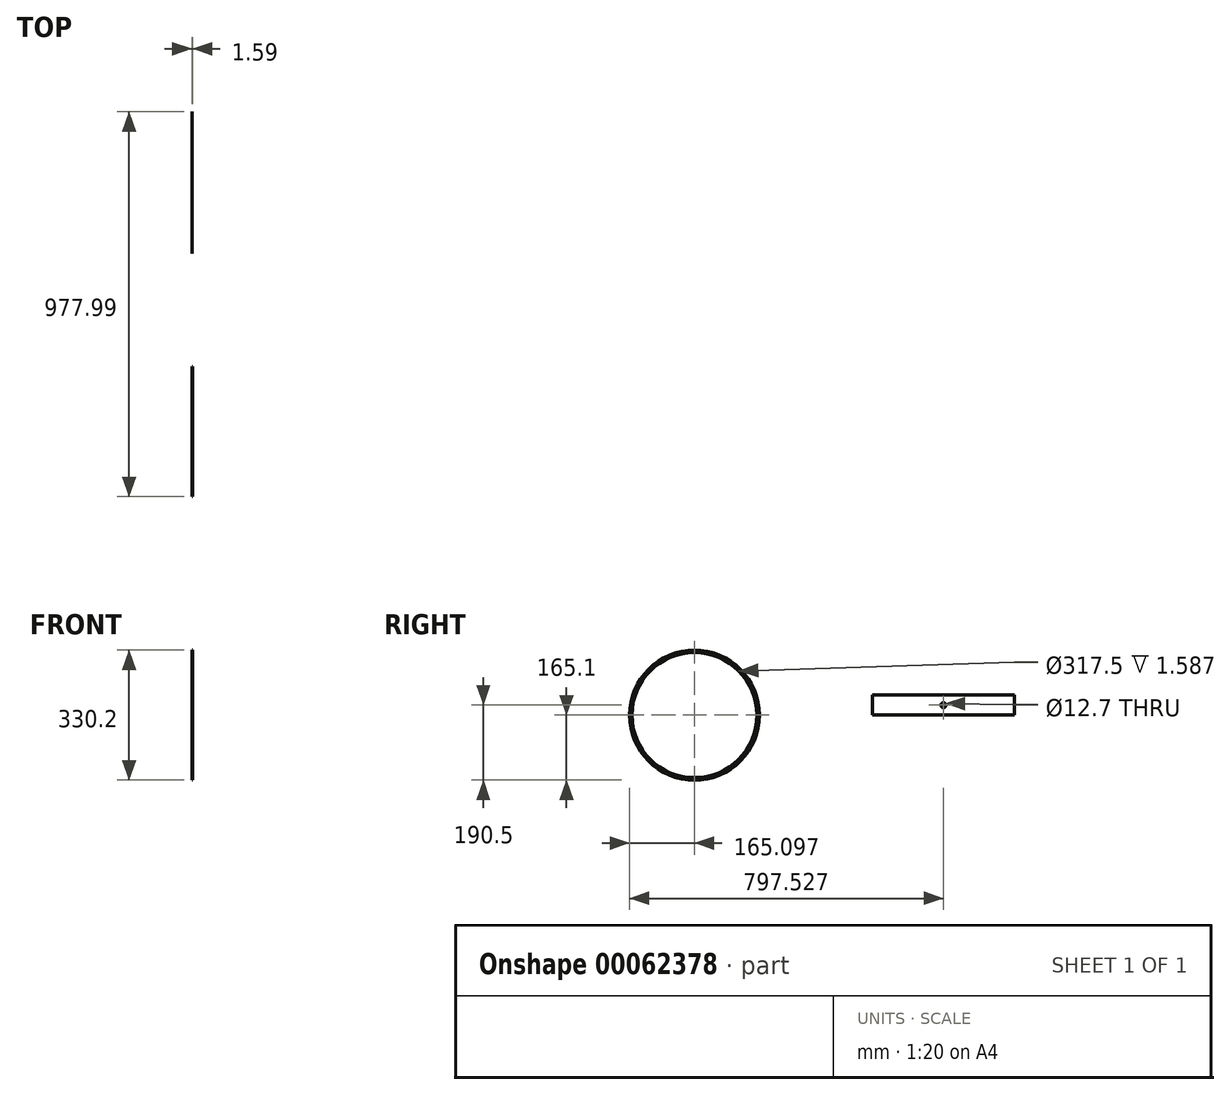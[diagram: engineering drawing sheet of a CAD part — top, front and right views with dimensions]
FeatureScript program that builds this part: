
annotation { "Feature Type Name" : "Feature", "Feature Type Description" : "" }
export const myFeature = defineFeature(function(context is Context, id is Id, definition is map)
    precondition{}
    {
        {
            var Q0;
            Q0=qCreatedBy(makeId("Right.planeOp"),FACE);
            var sketch = newSketch(context, id + "F0", { "sketchPlane" : qUnion([Q0])});
            skLineSegment(sketch, "E0.bottom", {"start": v(0, 0) * mm, "end": v(360.93, 0) * mm});
            skLineSegment(sketch, "E0.top", {"start": v(0, 50.8) * mm, "end": v(360.93, 50.8) * mm});
            skLineSegment(sketch, "E0.left", {"start": v(0, 0) * mm, "end": v(0, 50.8) * mm});
            skLineSegment(sketch, "E0.right", {"start": v(360.93, 0) * mm, "end": v(360.93, 50.8) * mm});
            skCircle(sketch, "E1", {"center": v(180.47, 25.4) * mm, "radius": 6.35 * mm});
            skPoint(sketch, "E1.centerSnap0", {"position": v(0, 25.4) * mm});
            skPoint(sketch, "E1.centerSnap1", {"position": v(180.47, 50.8) * mm});
            skSolve(sketch);
        }
        {
            var Q0;
            Q0=makeQuery(id+"F0.imprint","IMPRINT",FACE,{"disambiguationData":[TD([[makeQuery(id+"F0.imprint","IMPRINT",EDGE,{"derivedFrom":sQuery(id+"F0.wireOp",EDGE,"E0.bottom")}),1.0]])]});
            extrude(context, id + "F1", {"entities" : qUnion([Q0]), "depth" : 0.25 * mm});
        }
        {
            var Q0;
            Q0=qCreatedBy(makeId("Right.planeOp"),FACE);
            var sketch = newSketch(context, id + "F2", { "sketchPlane" : qUnion([Q0])});
            skCircle(sketch, "E2", {"center": v(-451.96, 0) * mm, "radius": 165.1 * mm});
            skCircle(sketch, "E3", {"center": v(-451.96, 0) * mm, "radius": 158.75 * mm});
            skSolve(sketch);
        }
        {
            var Q0;
            Q0=makeQuery(id+"F2.imprint","IMPRINT",FACE,{"disambiguationData":[TD([[makeQuery(id+"F2.imprint","IMPRINT",EDGE,{"derivedFrom":sQuery(id+"F2.wireOp",EDGE,"E2")}),1.0]])]});
            extrude(context, id + "F3", {"entities" : qUnion([Q0]), "depth" : 1.59 * mm});
        }
    });
